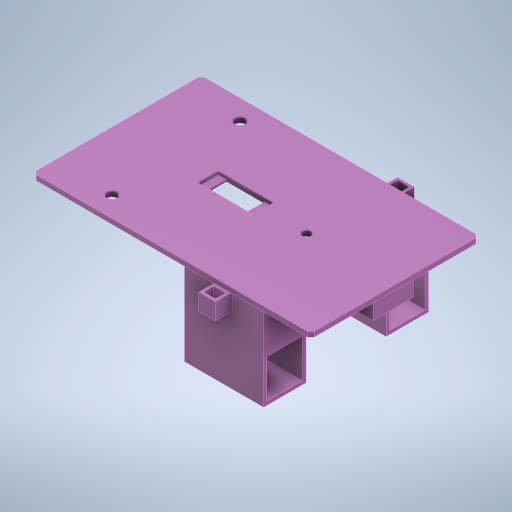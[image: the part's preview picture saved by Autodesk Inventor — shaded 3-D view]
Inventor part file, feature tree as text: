
AUTODESK INVENTOR PART (.ipt)
format: ipt  version: 2024 (Build 280153000, 153)  size: 408,064 bytes
history: native  units: in
note: dims shown in document units (in); Inventor stores cm internally (conversion verified against a paired STEP export)
features: extrude x14, sketch x14, chamfer x1
ambient origin geometry x8: Origin, YZ Plane, XZ Plane, XY Plane, X Axis, Y Axis, Z Axis, Center Point
bodies: Solid1 (feature_tree)
feature tree (29):
  extrude  "Extrusion1"  Depth=3.937in
  chamfer  "Chamfer1"  Distance=0.1181in
  extrude  "Extrusion2"  Depth=1.1811in
  extrude  "Extrusion3"  Depth=0.9173in
  extrude  "Extrusion4"  Depth=0.9173in
  extrude  "Extrusion5"  Depth=1.9685in TaperAngle=0.0deg
  extrude  "Extrusion6"  Depth=0.0787in
  extrude  "Extrusion7"  Depth=1.7913in TaperAngle=0.0deg
  extrude  "Extrusion8"  Depth=0.1969in
  extrude  "Extrusion9"  Depth=1.6142in
  extrude  "Extrusion10"  Depth=0.4724in
  extrude  "Extrusion11"  Depth=0.9449in
  extrude  "Extrusion12"  Depth=1.4961in
  extrude  "Extrusion13"  Depth=0.2441in
  extrude  "Extrusion14"  Depth=0.3937in
  sketch  "Sketch1"  dims[d0=6.4961in d1=3.937in d2=0.1181in d3=0.0in]
  sketch  "Sketch2"  dims[d4=0.0787in d5=0.0787in d6=45.0deg d7=1.1811in]
  sketch  "Sketch3"  dims[d8=0.9173in d9=1.7717in]
  sketch  "Sketch4"  dims[d10=0.0394in d11=0.9173in]
  sketch  "Sketch5"  dims[d12=0.0394in d13=1.9685in d14=0.0in]
  sketch  "Sketch6"  dims[d15=1.063in d16=0.0787in]
  sketch  "Sketch7"  dims[d17=0.0787in d18=1.7913in d19=0.0in]
  sketch  "Sketch8"  dims[d20=0.1969in d21=0.1969in]
  sketch  "Sketch9"  dims[d22=1.6142in d23=0.0in d24=1.7717in]
  sketch  "Sketch10"  dims[d25=0.4724in d26=0.4449in]
  sketch  "Sketch11"  dims[d27=0.4449in d28=0.9449in]
  sketch  "Sketch12"  dims[d29=1.4961in d30=1.4961in]
  sketch  "Sketch13"  dims[d31=0.2441in d32=0.2441in]
  sketch  "Sketch14"  dims[d33=1.7913in d34=0.0in d35=0.6476in d36=0.6476in d37=0.0827in d38=0.0in d39=0.7087in d40=0.6398in d41=0.6398in d42=0.0787in d43=0.0in d44=0.1181in d45=0.3937in d46=0.3937in d47=0.1969in d48=0.0787in d49=0.3937in d50=0.0in d51=0.1969in d52=0.1969in d53=0.3937in d54=0.3937in d55=0.0in d56=0.0591in d57=0.3346in d58=0.0in d59=0.3937in d60=0.0in d61=0.0591in d62=0.3346in d63=0.0in d64=0.1969in d65=0.3346in d66=0.0in d67=0.1181in d68=0.3937in d69=0.3937in d70=0.1969in d71=0.0787in d72=0.3937in d73=0.0in]
